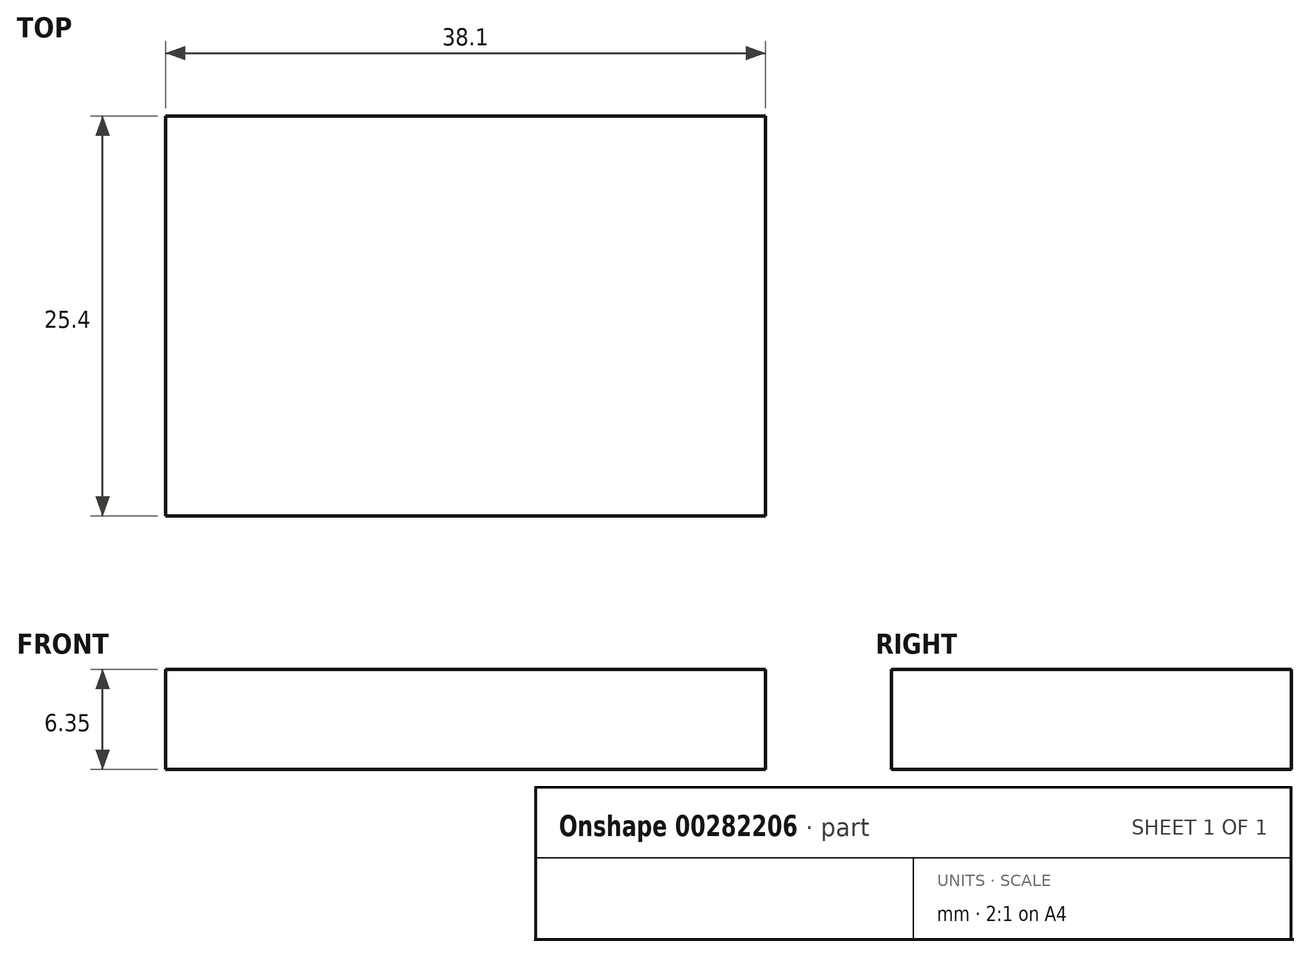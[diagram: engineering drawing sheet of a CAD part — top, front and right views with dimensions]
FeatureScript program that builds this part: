
annotation { "Feature Type Name" : "Feature", "Feature Type Description" : "" }
export const myFeature = defineFeature(function(context is Context, id is Id, definition is map)
    precondition{}
    {
        {
            var Q0;
            Q0=qCreatedBy(makeId("Top.planeOp"),FACE);
            var sketch = newSketch(context, id + "F0", { "sketchPlane" : qUnion([Q0])});
            skLineSegment(sketch, "E0.bottom", {"start": v(0, 0) * mm, "end": v(38.1, 0) * mm});
            skLineSegment(sketch, "E0.top", {"start": v(0, 25.4) * mm, "end": v(38.1, 25.4) * mm});
            skLineSegment(sketch, "E0.left", {"start": v(0, 0) * mm, "end": v(0, 25.4) * mm});
            skLineSegment(sketch, "E0.right", {"start": v(38.1, 0) * mm, "end": v(38.1, 25.4) * mm});
            skSolve(sketch);
        }
        {
            var Q0;
            Q0 = qSketchRegion(id + "F0", true);
            extrude(context, id + "F1", {"entities" : qUnion([Q0]), "depth" : 6.35 * mm});
        }
    });
